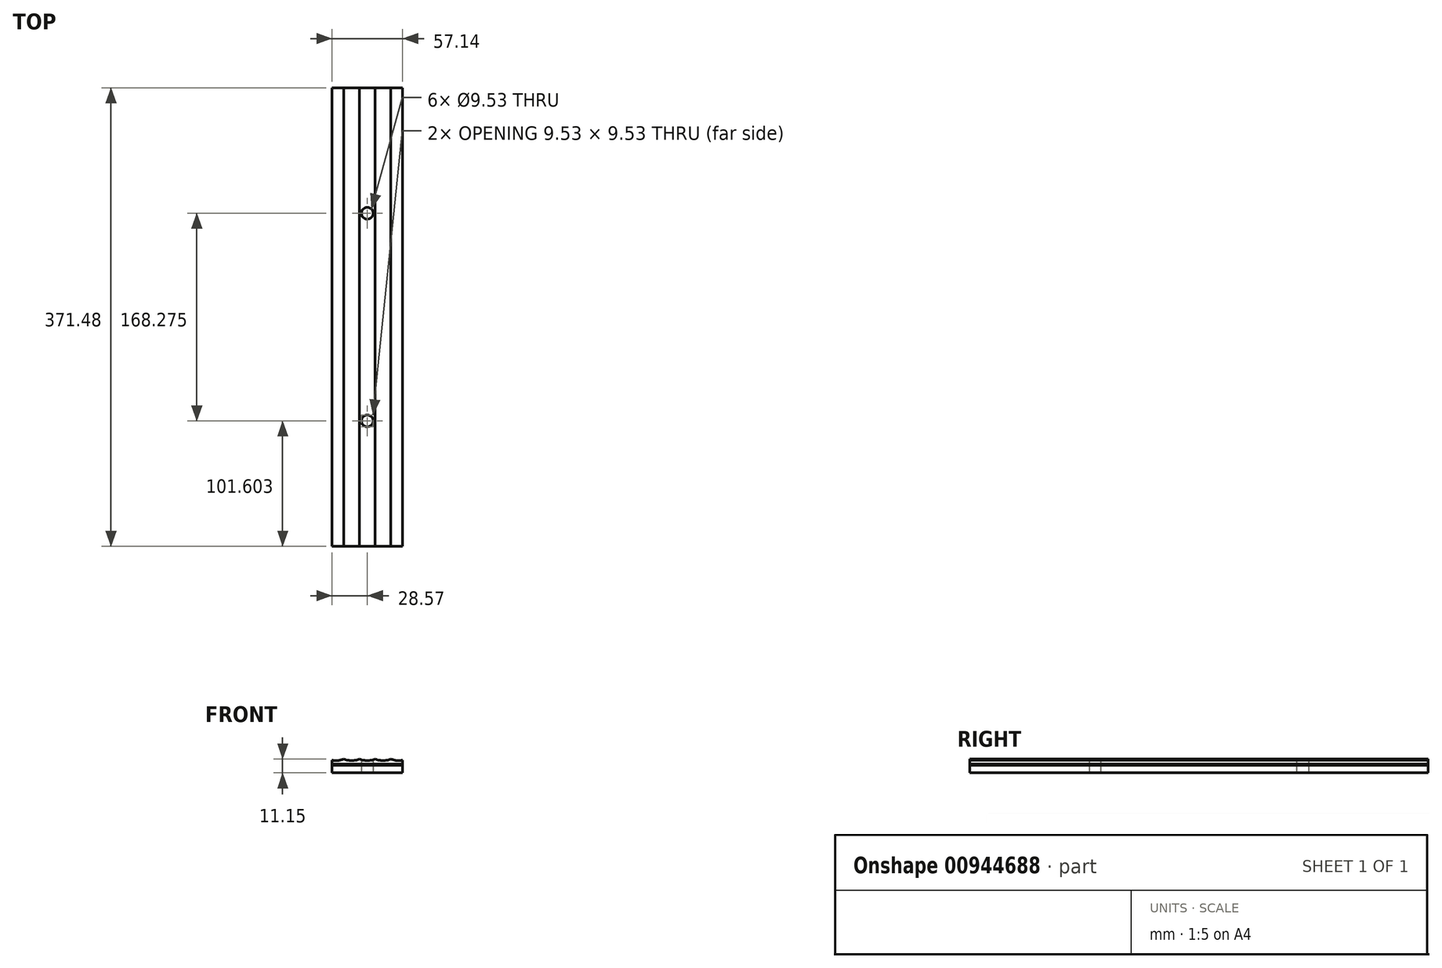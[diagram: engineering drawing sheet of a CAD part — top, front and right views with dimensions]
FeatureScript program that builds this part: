
annotation { "Feature Type Name" : "Feature", "Feature Type Description" : "" }
export const myFeature = defineFeature(function(context is Context, id is Id, definition is map)
    precondition{}
    {
        {
            var Q0;
            Q0=qCreatedBy(makeId("Front.planeOp"),FACE);
            var sketch = newSketch(context, id + "F0", { "sketchPlane" : qUnion([Q0])});
            skLineSegment(sketch, "E0.bottom", {"start": v(28.58, 0) * mm, "end": v(0, 0) * mm});
            skLineSegment(sketch, "E0.top", {"start": v(28.58, 6) * mm, "end": v(0, 6) * mm});
            skLineSegment(sketch, "E0.left", {"start": v(28.58, 0) * mm, "end": v(28.58, 6) * mm});
            skLineSegment(sketch, "E1.top", {"start": v(28.58, 7.08) * mm, "end": v(0, 7.08) * mm});
            skLineSegment(sketch, "E1.left", {"start": v(28.58, 6) * mm, "end": v(28.58, 7.08) * mm});
            skLineSegment(sketch, "E2", {"start": v(28.58, 7.08) * mm, "end": v(28.58, 11.15) * mm});
            skArc(sketch, "E3.4.0.0", {"start": v(28.58, 10.25) * mm, "mid": v(23.75, 10.04) * mm, "end": v(19.05, 11.15) * mm});
            skArc(sketch, "E3.5.0.0", {"start": v(19.05, 11.15) * mm, "mid": v(12.7, 9.96) * mm, "end": v(6.35, 11.15) * mm});
            skArc(sketch, "E3.6.0.0", {"start": v(6.35, 11.15) * mm, "mid": v(3.23, 10.26) * mm, "end": v(0, 9.96) * mm});
            skLineSegment(sketch, "E3.direction1", {"start": v(-105.06, -36.9) * mm, "end": v(-92.36, -36.9) * mm, "construction": true});
            skPoint(sketch, "E4.orphan", {"position": v(-93.66, 11.07) * mm});
            skLineSegment(sketch, "E5", {"start": v(0, 0) * mm, "end": v(0, 9.96) * mm, "construction": true});
            skLineSegment(sketch, "E6.trimOffspring", {"start": v(0, 27.6) * mm, "end": v(0, 43.35) * mm, "construction": true});
            skLineSegment(sketch, "E7", {"start": v(19.05, 11.15) * mm, "end": v(19.05, 7.08) * mm, "construction": true});
            skLineSegment(sketch, "E8", {"start": v(6.35, 11.15) * mm, "end": v(23.81, 11.15) * mm, "construction": true});
            skLineSegment(sketch, "E9.MirrorCS", {"start": v(-28.58, 6) * mm, "end": v(-28.58, 7.08) * mm});
            skLineSegment(sketch, "E10.MirrorCS", {"start": v(-28.58, 6) * mm, "end": v(0, 6) * mm});
            skLineSegment(sketch, "E11.MirrorCS", {"start": v(-28.58, 7.08) * mm, "end": v(-28.58, 11.15) * mm});
            skLineSegment(sketch, "E12.MirrorCS", {"start": v(-19.05, 11.15) * mm, "end": v(-19.05, 7.08) * mm, "construction": true});
            skLineSegment(sketch, "E13.MirrorCS", {"start": v(-28.58, 7.08) * mm, "end": v(0, 7.08) * mm});
            skLineSegment(sketch, "E14.MirrorCS", {"start": v(-28.58, 0) * mm, "end": v(0, 0) * mm});
            skArc(sketch, "E15.MirrorCS", {"start": v(-19.05, 11.15) * mm, "mid": v(-12.7, 9.96) * mm, "end": v(-6.35, 11.15) * mm});
            skLineSegment(sketch, "E16.MirrorCS", {"start": v(-6.35, 11.15) * mm, "end": v(-23.81, 11.15) * mm, "construction": true});
            skArc(sketch, "E17.MirrorCS", {"start": v(-28.58, 10.25) * mm, "mid": v(-23.75, 10.04) * mm, "end": v(-19.05, 11.15) * mm});
            skLineSegment(sketch, "E18.MirrorCS", {"start": v(-28.58, 0) * mm, "end": v(-28.58, 6) * mm});
            skArc(sketch, "E19.MirrorCS", {"start": v(-6.35, 11.15) * mm, "mid": v(-3.23, 10.26) * mm, "end": v(0, 9.96) * mm});
            skPoint(sketch, "E20.orphan", {"position": v(30.96, 9.98) * mm});
            skPoint(sketch, "E21.orphan", {"position": v(-30.96, 9.98) * mm});
            skPoint(sketch, "E22.orphan", {"position": v(-31.75, 11.15) * mm});
            skPoint(sketch, "E23.orphan", {"position": v(31.75, 11.15) * mm});
            skSolve(sketch);
        }
        {
            var Q0;
            Q0=makeQuery(id+"F0.imprint","IMPRINT",FACE,{"disambiguationData":[TD([[makeQuery(id+"F0.imprint","IMPRINT",EDGE,{"derivedFrom":sQuery(id+"F0.wireOp",EDGE,"E0.bottom")}),-1.0]])]});
            var Q1;
            Q1=sQuery(id+"F0.wireOp",EDGE,"E0.left");
            var Q2;
            Q2=sQuery(id+"F0.wireOp",EDGE,"E0.bottom");
            var Q3;
            Q3=sQuery(id+"F0.wireOp",EDGE,"E0.top");
            var Q4;
            Q4=sQuery(id+"F0.wireOp",EDGE,"E0.right");
            extrude(context, id + "F1", {"entities" : qUnion([Q0]), "surfaceEntities" : qUnion([Q1, Q2, Q3, Q4]), "endBound" : BoundingType.SYMMETRIC, "depth" : 371.47 * mm, "offsetDistance" : 25.4 * mm});
        }
        {
            var Q0;
            Q0=makeQuery(id+"F0.imprint","IMPRINT",FACE,{"disambiguationData":[TD([[makeQuery(id+"F0.imprint","IMPRINT",EDGE,{"derivedFrom":sQuery(id+"F0.wireOp",EDGE,"E0.top")}),-1.0]])]});
            extrude(context, id + "F2", {"entities" : qUnion([Q0]), "endBound" : BoundingType.SYMMETRIC, "depth" : 371.47 * mm, "offsetDistance" : 25.4 * mm});
        }
        {
            var Q0;
            {var subQ3=sQuery(id+"F0.wireOp",EDGE,"E1.top");Q0=makeQuery(id+"F0.imprint","IMPRINT",FACE,{"disambiguationData":[TD([[makeQuery(id+"F0.imprint","IMPRINT",EDGE,{"derivedFrom":subQ3}),-1.0]])]});}
            extrude(context, id + "F3", {"entities" : qUnion([Q0]), "endBound" : BoundingType.SYMMETRIC, "depth" : 371.47 * mm, "offsetDistance" : 25.4 * mm});
        }
        {
            var Q0;
            Q0=qCreatedBy(makeId("Top.planeOp"),FACE);
            var sketch = newSketch(context, id + "F4", { "sketchPlane" : qUnion([Q0])});
            skLineSegment(sketch, "E24", {"start": v(0, 749.3) * mm, "end": v(0, -749.3) * mm, "construction": true});
            skPoint(sketch, "E25", {"position": v(0, 0) * mm});
            skCircle(sketch, "E26", {"center": v(0, 84.14) * mm, "radius": 4.76 * mm});
            skLineSegment(sketch, "E27", {"start": v(0, 0) * mm, "end": v(-13.94, 0) * mm, "construction": true});
            skCircle(sketch, "E28.MirrorC", {"center": v(0, -84.14) * mm, "radius": 4.76 * mm});
            skSolve(sketch);
        }
        {
            var Q0;
            Q0=qSketchRegion(id+"F4",true);
            extrude(context, id + "F5", {"entities" : qUnion([Q0]), "operationType" : NewBodyOperationType.REMOVE, "depth" : 25.4 * mm, "offsetDistance" : 25.4 * mm});
        }
    });
